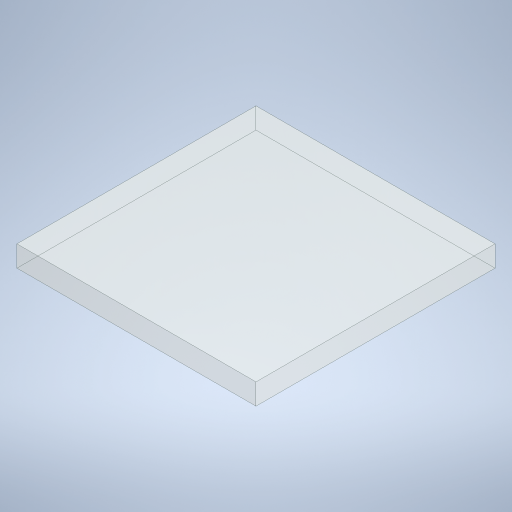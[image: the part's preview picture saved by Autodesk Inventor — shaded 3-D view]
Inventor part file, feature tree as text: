
AUTODESK INVENTOR PART (.ipt)
format: ipt  version: 2024 (Build 280153000, 153)  size: 220,160 bytes
history: native  units: mm
features: extrude x1, sketch x1
ambient origin geometry x8: Origin, YZ Plane, XZ Plane, XY Plane, X Axis, Y Axis, Z Axis, Center Point
bodies: Volumenkörper1 (feature_tree)
feature tree (2):
  extrude  "Extrusion1"  Depth=25.0mm
  sketch  "Skizze1"  dims[d0=25.0mm d1=25.0mm d2=2.2mm d3=0.0mm]
